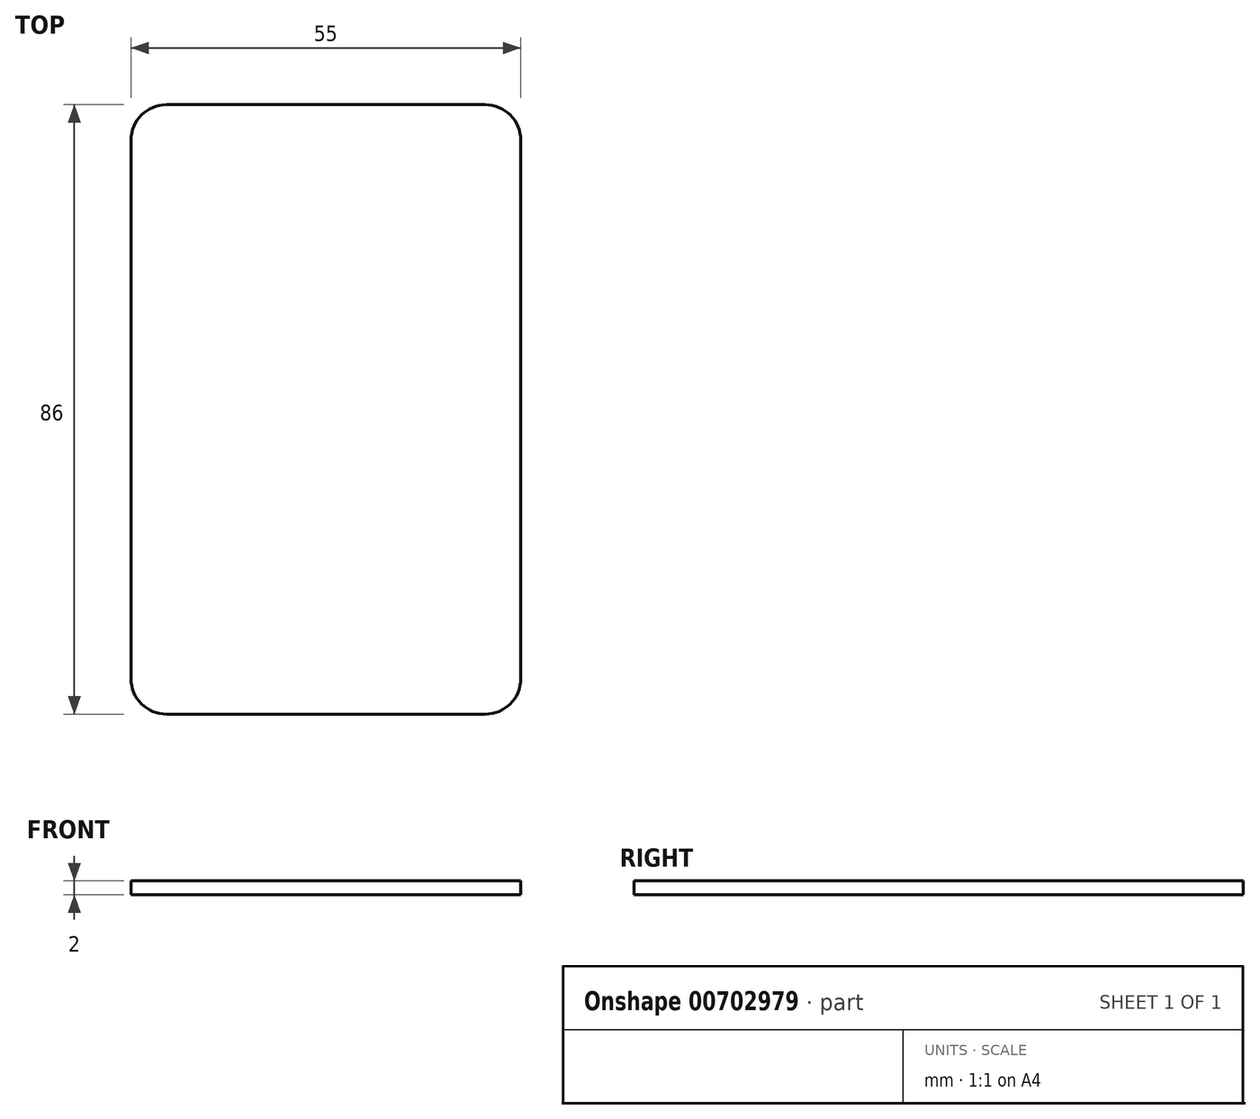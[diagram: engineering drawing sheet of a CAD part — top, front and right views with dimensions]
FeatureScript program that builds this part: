
annotation { "Feature Type Name" : "Feature", "Feature Type Description" : "" }
export const myFeature = defineFeature(function(context is Context, id is Id, definition is map)
    precondition{}
    {
        {
            var Q0;
            Q0=qCreatedBy(makeId("Top.planeOp"),FACE);
            var sketch = newSketch(context, id + "F0", { "sketchPlane" : qUnion([Q0])});
            skLineSegment(sketch, "E0.bottom", {"start": v(22.5, -43) * mm, "end": v(-22.5, -43) * mm});
            skLineSegment(sketch, "E0.top", {"start": v(22.5, 43) * mm, "end": v(-22.5, 43) * mm});
            skLineSegment(sketch, "E0.left", {"start": v(27.5, -38) * mm, "end": v(27.5, 38) * mm});
            skLineSegment(sketch, "E0.right", {"start": v(-27.5, -38) * mm, "end": v(-27.5, 38) * mm});
            skPoint(sketch, "E0.middle", {"position": v(0, 0) * mm});
            skPoint(sketch, "E1.visualSharp", {"position": v(-27.5, 43) * mm});
            skArc(sketch, "E1.filletArc", {"start": v(-22.5, 43) * mm, "mid": v(-26.04, 41.54) * mm, "end": v(-27.5, 38) * mm});
            skPoint(sketch, "E2.visualSharp", {"position": v(27.5, 43) * mm});
            skArc(sketch, "E2.filletArc", {"start": v(27.5, 38) * mm, "mid": v(26.04, 41.54) * mm, "end": v(22.5, 43) * mm});
            skPoint(sketch, "E3.visualSharp", {"position": v(27.5, -43) * mm});
            skArc(sketch, "E3.filletArc", {"start": v(22.5, -43) * mm, "mid": v(26.04, -41.54) * mm, "end": v(27.5, -38) * mm});
            skPoint(sketch, "E4.visualSharp", {"position": v(-27.5, -43) * mm});
            skArc(sketch, "E4.filletArc", {"start": v(-27.5, -38) * mm, "mid": v(-26.04, -41.54) * mm, "end": v(-22.5, -43) * mm});
            skSolve(sketch);
        }
        {
            var Q0;
            Q0=makeQuery(id+"F0.imprint","IMPRINT",FACE,{"disambiguationData":[TD([[makeQuery(id+"F0.imprint","IMPRINT",EDGE,{"derivedFrom":sQuery(id+"F0.wireOp",EDGE,"E0.bottom")}),-1.0]])]});
            extrude(context, id + "F1", {"entities" : qUnion([Q0]), "depth" : 2 * mm, "offsetDistance" : 25 * mm});
        }
    });
